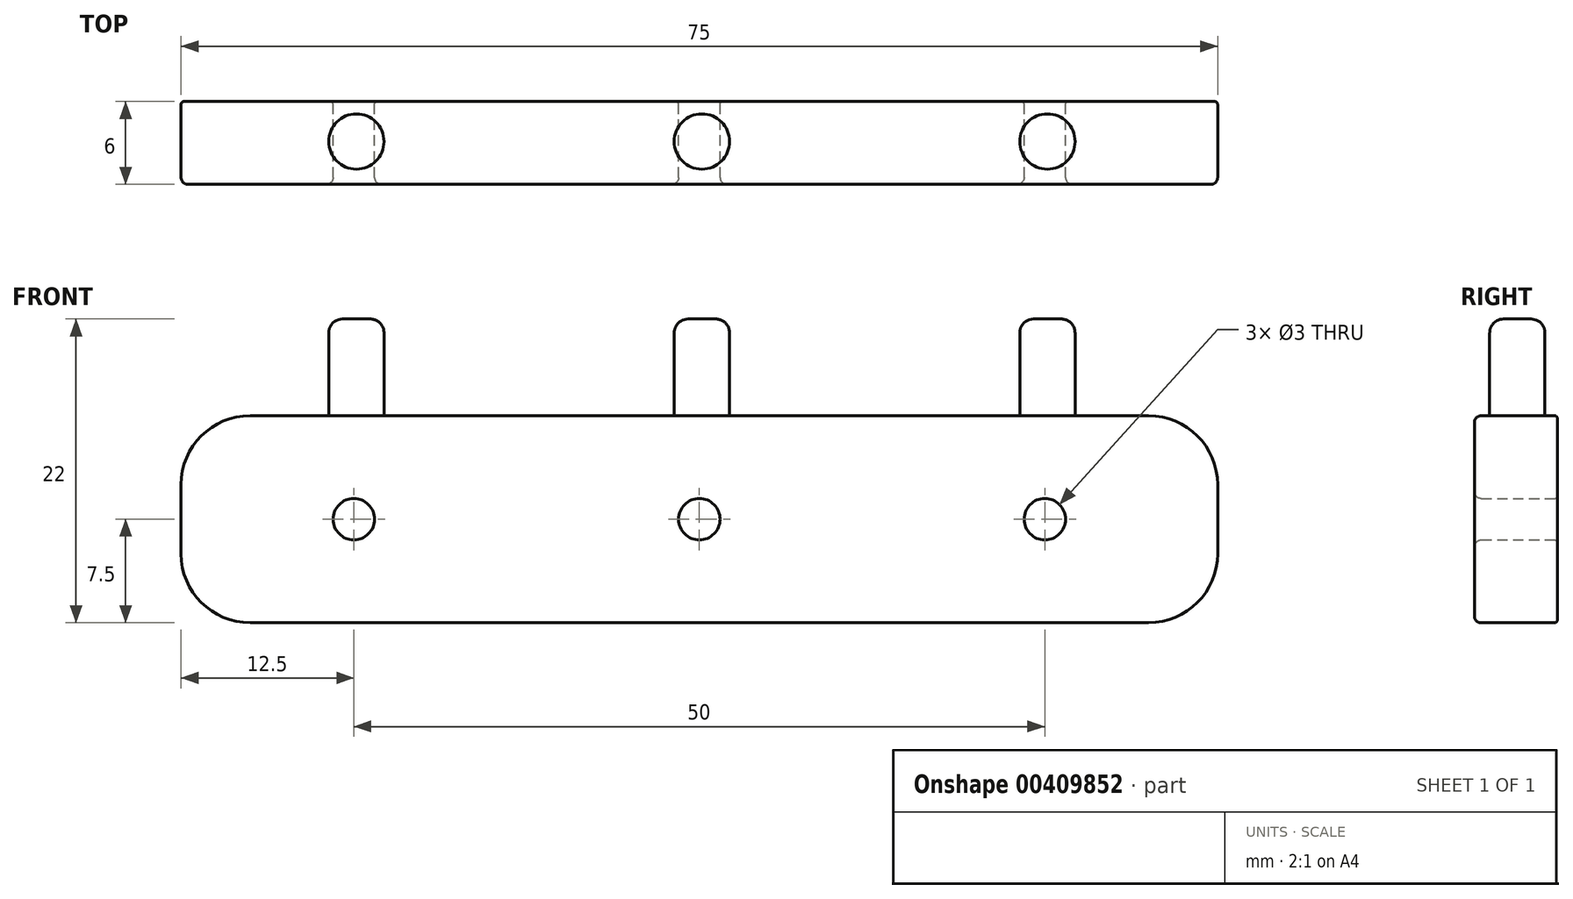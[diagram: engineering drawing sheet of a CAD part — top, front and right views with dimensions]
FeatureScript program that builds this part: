
annotation { "Feature Type Name" : "Feature", "Feature Type Description" : "" }
export const myFeature = defineFeature(function(context is Context, id is Id, definition is map)
    precondition{}
    {
        {
            var Q0;
            Q0=qCreatedBy(makeId("Front.planeOp"),FACE);
            var sketch = newSketch(context, id + "F0", { "sketchPlane" : qUnion([Q0])});
            skLineSegment(sketch, "E0.bottom", {"start": v(32.5, 7.5) * mm, "end": v(-32.5, 7.5) * mm});
            skLineSegment(sketch, "E0.top", {"start": v(32.5, -7.5) * mm, "end": v(-32.5, -7.5) * mm});
            skLineSegment(sketch, "E0.left", {"start": v(37.5, 2.5) * mm, "end": v(37.5, -2.5) * mm});
            skLineSegment(sketch, "E0.right", {"start": v(-37.5, 2.5) * mm, "end": v(-37.5, -2.5) * mm});
            skPoint(sketch, "E0.middle", {"position": v(0, 0) * mm});
            skCircle(sketch, "E1", {"center": v(-25, 0) * mm, "radius": 1.5 * mm});
            skCircle(sketch, "E2.1.0.0", {"center": v(0, 0) * mm, "radius": 1.5 * mm});
            skCircle(sketch, "E2.2.0.0", {"center": v(25, 0) * mm, "radius": 1.5 * mm});
            skLineSegment(sketch, "E2.direction1", {"start": v(-25, 0) * mm, "end": v(0, 0) * mm, "construction": true});
            skPoint(sketch, "E3.visualSharp", {"position": v(-37.5, 7.5) * mm});
            skArc(sketch, "E3.filletArc", {"start": v(-32.5, 7.5) * mm, "mid": v(-36.04, 6.04) * mm, "end": v(-37.5, 2.5) * mm});
            skPoint(sketch, "E4.visualSharp", {"position": v(37.5, 7.5) * mm});
            skArc(sketch, "E4.filletArc", {"start": v(37.5, 2.5) * mm, "mid": v(36.04, 6.04) * mm, "end": v(32.5, 7.5) * mm});
            skPoint(sketch, "E5.visualSharp", {"position": v(37.5, -7.5) * mm});
            skArc(sketch, "E5.filletArc", {"start": v(32.5, -7.5) * mm, "mid": v(36.04, -6.04) * mm, "end": v(37.5, -2.5) * mm});
            skPoint(sketch, "E6.visualSharp", {"position": v(-37.5, -7.5) * mm});
            skArc(sketch, "E6.filletArc", {"start": v(-37.5, -2.5) * mm, "mid": v(-36.04, -6.04) * mm, "end": v(-32.5, -7.5) * mm});
            skSolve(sketch);
        }
        {
            var Q0;
            Q0=qSketchRegion(id+"F0",true);
            extrude(context, id + "F1", {"entities" : qUnion([Q0]), "depth" : 6 * mm});
        }
        {
            var Q0;
            Q0=makeQuery(id+"F1.opExtrude","CAP_FACE",FACE,{"disambiguationData":[OSD([sQuery(id+"F0.wireOp",EDGE,"E0.bottom"),sQuery(id+"F0.wireOp",EDGE,"E0.top"),sQuery(id+"F0.wireOp",EDGE,"E0.left"),sQuery(id+"F0.wireOp",EDGE,"E0.right"),sQuery(id+"F0.wireOp",EDGE,"E1"),sQuery(id+"F0.wireOp",EDGE,"E2.1.0.0"),sQuery(id+"F0.wireOp",EDGE,"E2.2.0.0"),sQuery(id+"F0.wireOp",EDGE,"E3.filletArc"),sQuery(id+"F0.wireOp",EDGE,"E4.filletArc"),sQuery(id+"F0.wireOp",EDGE,"E5.filletArc"),sQuery(id+"F0.wireOp",EDGE,"E6.filletArc")])],"isStart":false});
            fillet(context, id + "F2", {"entities" : qUnion([Q0]), "radius" : .5 * mm, "tangentPropagation" : true, "allowEdgeOverflow" : false});
        }
        {
            var Q0;
            Q0=makeQuery(id+"F1.opExtrude","CAP_FACE",FACE,{"disambiguationData":[OSD([sQuery(id+"F0.wireOp",EDGE,"E0.bottom"),sQuery(id+"F0.wireOp",EDGE,"E0.top"),sQuery(id+"F0.wireOp",EDGE,"E0.left"),sQuery(id+"F0.wireOp",EDGE,"E0.right"),sQuery(id+"F0.wireOp",EDGE,"E1"),sQuery(id+"F0.wireOp",EDGE,"E2.1.0.0"),sQuery(id+"F0.wireOp",EDGE,"E2.2.0.0"),sQuery(id+"F0.wireOp",EDGE,"E3.filletArc"),sQuery(id+"F0.wireOp",EDGE,"E4.filletArc"),sQuery(id+"F0.wireOp",EDGE,"E5.filletArc"),sQuery(id+"F0.wireOp",EDGE,"E6.filletArc")])],"isStart":true});
            fillet(context, id + "F3", {"entities" : qUnion([Q0]), "radius" : .2 * mm, "tangentPropagation" : true, "allowEdgeOverflow" : false});
        }
        {
            var Q0;
            Q0=makeQuery(id+"F1.opExtrude","SWEPT_FACE",FACE,{"disambiguationData":[OSD([sQuery(id+"F0.wireOp",EDGE,"E0.bottom")])]});
            var sketch = newSketch(context, id + "F4", { "sketchPlane" : qUnion([Q0])});
            skCircle(sketch, "E7", {"center": v(-24.82, -2.9) * mm, "radius": 2 * mm});
            skCircle(sketch, "E8.1.0.0", {"center": v(0.18, -2.9) * mm, "radius": 2 * mm});
            skCircle(sketch, "E8.2.0.0", {"center": v(25.18, -2.9) * mm, "radius": 2 * mm});
            skLineSegment(sketch, "E8.direction1", {"start": v(-24.82, -2.9) * mm, "end": v(0.18, -2.9) * mm, "construction": true});
            skSolve(sketch);
        }
        {
            var Q0;
            Q0=makeQuery(id+"F4.imprint","IMPRINT",FACE,{"disambiguationData":[TD([[makeQuery(id+"F4.imprint","IMPRINT",EDGE,{"derivedFrom":sQuery(id+"F4.wireOp",EDGE,"E7")}),1.0]])]});
            var Q1;
            Q1=makeQuery(id+"F4.imprint","IMPRINT",FACE,{"disambiguationData":[TD([[makeQuery(id+"F4.imprint","IMPRINT",EDGE,{"derivedFrom":sQuery(id+"F4.wireOp",EDGE,"E8.1.0.0")}),1.0]])]});
            var Q2;
            Q2=makeQuery(id+"F4.imprint","IMPRINT",FACE,{"disambiguationData":[TD([[makeQuery(id+"F4.imprint","IMPRINT",EDGE,{"derivedFrom":sQuery(id+"F4.wireOp",EDGE,"E8.2.0.0")}),1.0]])]});
            extrude(context, id + "F5", {"entities" : qUnion([Q0, Q1, Q2]), "operationType" : NewBodyOperationType.ADD, "depth" : 7 * mm});
        }
        {
            var Q0;
            Q0=makeQuery(id+"F5.opExtrude","CAP_EDGE",EDGE,{"disambiguationData":[OSD([sQuery(id+"F4.wireOp",EDGE,"E7")])],"isStart":false});
            var Q1;
            Q1=makeQuery(id+"F5.opExtrude","CAP_EDGE",EDGE,{"disambiguationData":[OSD([sQuery(id+"F4.wireOp",EDGE,"E8.1.0.0")])],"isStart":false});
            var Q2;
            Q2=makeQuery(id+"F5.opExtrude","CAP_FACE",FACE,{"disambiguationData":[OSD([sQuery(id+"F4.wireOp",EDGE,"E8.2.0.0")])],"isStart":false});
            fillet(context, id + "F6", {"entities" : qUnion([Q0, Q1, Q2]), "radius" : 1 * mm, "tangentPropagation" : true, "allowEdgeOverflow" : false});
        }
    });
